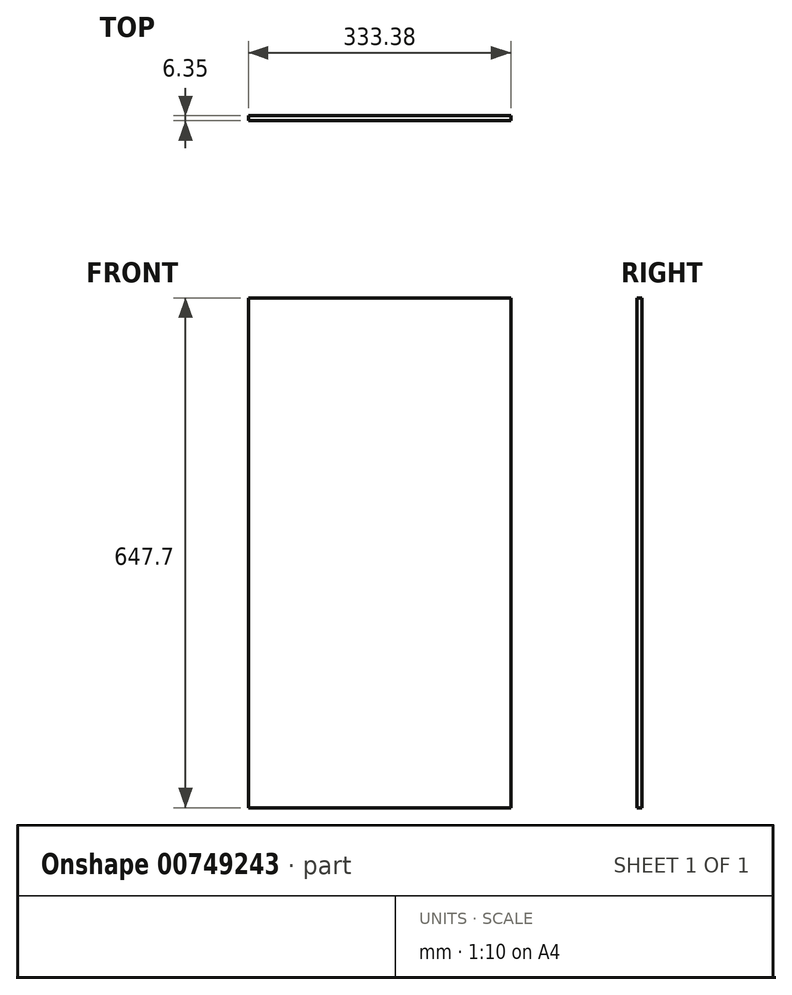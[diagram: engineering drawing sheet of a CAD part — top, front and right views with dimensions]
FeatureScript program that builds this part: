
annotation { "Feature Type Name" : "Feature", "Feature Type Description" : "" }
export const myFeature = defineFeature(function(context is Context, id is Id, definition is map)
    precondition{}
    {
        {
            var Q0;
            Q0=qCreatedBy(makeId("Front.planeOp"),FACE);
            var sketch = newSketch(context, id + "F0", { "sketchPlane" : qUnion([Q0])});
            skLineSegment(sketch, "E0.bottom", {"start": v(166.69, 323.85) * mm, "end": v(-166.69, 323.85) * mm});
            skLineSegment(sketch, "E0.top", {"start": v(166.69, -323.85) * mm, "end": v(-166.69, -323.85) * mm});
            skLineSegment(sketch, "E0.left", {"start": v(166.69, 323.85) * mm, "end": v(166.69, -323.85) * mm});
            skLineSegment(sketch, "E0.right", {"start": v(-166.69, 323.85) * mm, "end": v(-166.69, -323.85) * mm});
            skPoint(sketch, "E0.middle", {"position": v(0, 0) * mm});
            skSolve(sketch);
        }
        {
            var Q0;
            Q0 = qSketchRegion(id + "F0", true);
            extrude(context, id + "F1", {"entities" : qUnion([Q0]), "depth" : 6.35 * mm, "offsetDistance" : 25.4 * mm});
        }
    });
